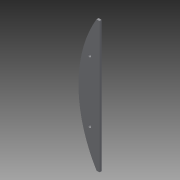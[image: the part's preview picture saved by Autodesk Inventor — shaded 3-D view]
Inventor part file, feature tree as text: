
AUTODESK INVENTOR PART (.ipt)
format: ipt  version: 2015 (Build 190159000, 159)  size: 80,384 bytes
history: native  units: mm
features: extrude x2, sketch x1
ambient origin geometry x8: Origin, YZ Plane, XZ Plane, XY Plane, X Axis, Y Axis, Z Axis, Center Point
bodies: Solid1 (feature_tree)
feature tree (3):
  sketch  "Sketch1"  dims[d2=3.0mm d3=3.0mm d11=2.0mm d12=0.0mm d13=35.0mm d14=35.35mm d17=3.0mm d18=3.0mm d19=2.0mm d20=0.0mm]
  extrude  "Extrusion1"  Depth=2.0mm
  extrude  "Extrusion2"  Depth=2.0mm TaperAngle=0.0deg
